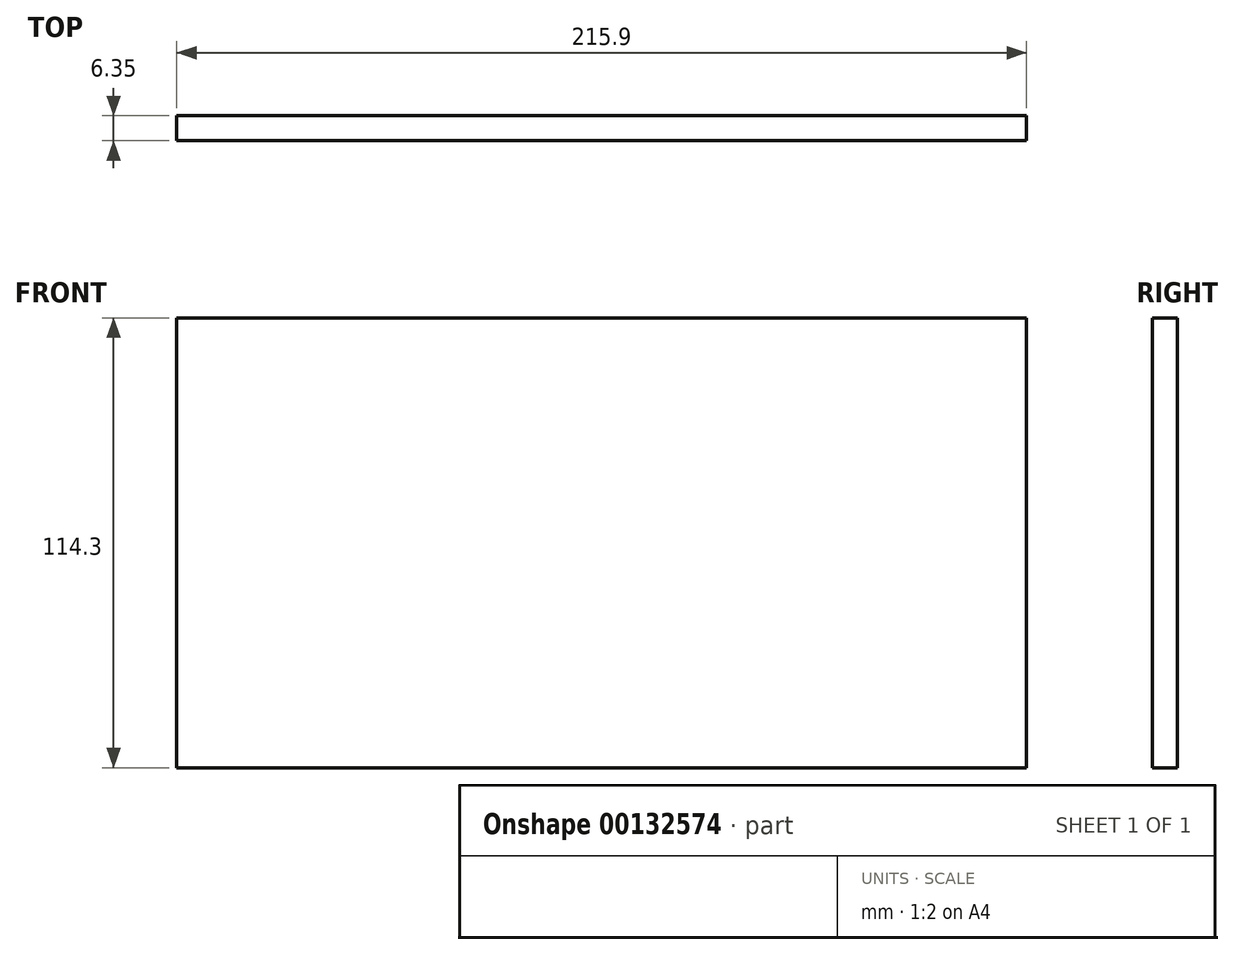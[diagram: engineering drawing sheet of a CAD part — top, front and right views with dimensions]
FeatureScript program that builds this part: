
annotation { "Feature Type Name" : "Feature", "Feature Type Description" : "" }
export const myFeature = defineFeature(function(context is Context, id is Id, definition is map)
    precondition{}
    {
        {
            var Q0;
            Q0=qCreatedBy(makeId("Front.planeOp"),FACE);
            var sketch = newSketch(context, id + "F0", { "sketchPlane" : qUnion([Q0])});
            skLineSegment(sketch, "E0.bottom", {"start": v(-76.12, 71.3) * mm, "end": v(139.78, 71.3) * mm});
            skLineSegment(sketch, "E0.top", {"start": v(-76.12, -43) * mm, "end": v(139.78, -43) * mm});
            skLineSegment(sketch, "E0.left", {"start": v(-76.12, 71.3) * mm, "end": v(-76.12, -43) * mm});
            skLineSegment(sketch, "E0.right", {"start": v(139.78, 71.3) * mm, "end": v(139.78, -43) * mm});
            skSolve(sketch);
        }
        {
            var Q0;
            Q0 = qSketchRegion(id + "F0", true);
            extrude(context, id + "F1", {"entities" : qUnion([Q0]), "depth" : 6.35 * mm});
        }
    });
